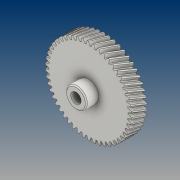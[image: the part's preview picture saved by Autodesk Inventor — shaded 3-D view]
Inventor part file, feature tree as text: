
AUTODESK INVENTOR PART (.ipt)
format: ipt  version: 2021 (Build 250183000, 183)  size: 741,888 bytes
history: native  units: mm (DEFAULTED — no unit token found)
features: extrude x3, plane x3, other x3, sketch x3, chamfer x1
ambient origin geometry x8: Origin, YZ Plane, XZ Plane, XY Plane, X Axis, Y Axis, Z Axis, Center Point
bodies: Solid1 (feature_tree)
feature tree (13):
  extrude  "Extrusion1"  Depth=15.0mm TaperAngle=0.0deg
  plane  "Work Plane2"
  plane  "Work Plane8"
  plane  "Work Plane9"
  other  "Spur Gear"
  sketch  "Sketch3"  dims[d16=60.0mm d17=0.0mm d34=0.628319mm d39=0.0mm d41=0.0mm d43=60.0mm d46=60.0mm d47=0.0mm d48=0.0mm d49=10.0mm d51=5.0mm d52=0.0mm d53=0.0mm d54=12.0mm d55=0.0mm d56=1.0mm d57=2.0mm d58=45.0deg]
  extrude  "Extrusion2"  Depth=10.0mm TaperAngle=0.0deg
  extrude  "Extrusion3"  Depth=5.0mm TaperAngle=0.0deg
  chamfer  "Chamfer1"  [1 undecoded]
  sketch  "Sketch1"  dims[d0=83.093334mm d1=15.0mm d2=0.0mm]
  sketch  "Sketch2"  dims[d3=79.813333mm d4=10.0mm d5=0.0mm]
  other  "Srf1"
  other  "Pitch Diameter"
note: 1 required parameter value undecoded (feature->parameter linkage not recoverable at this tier; creation-order binding heuristic only, values carry confidence <= 0.55)
